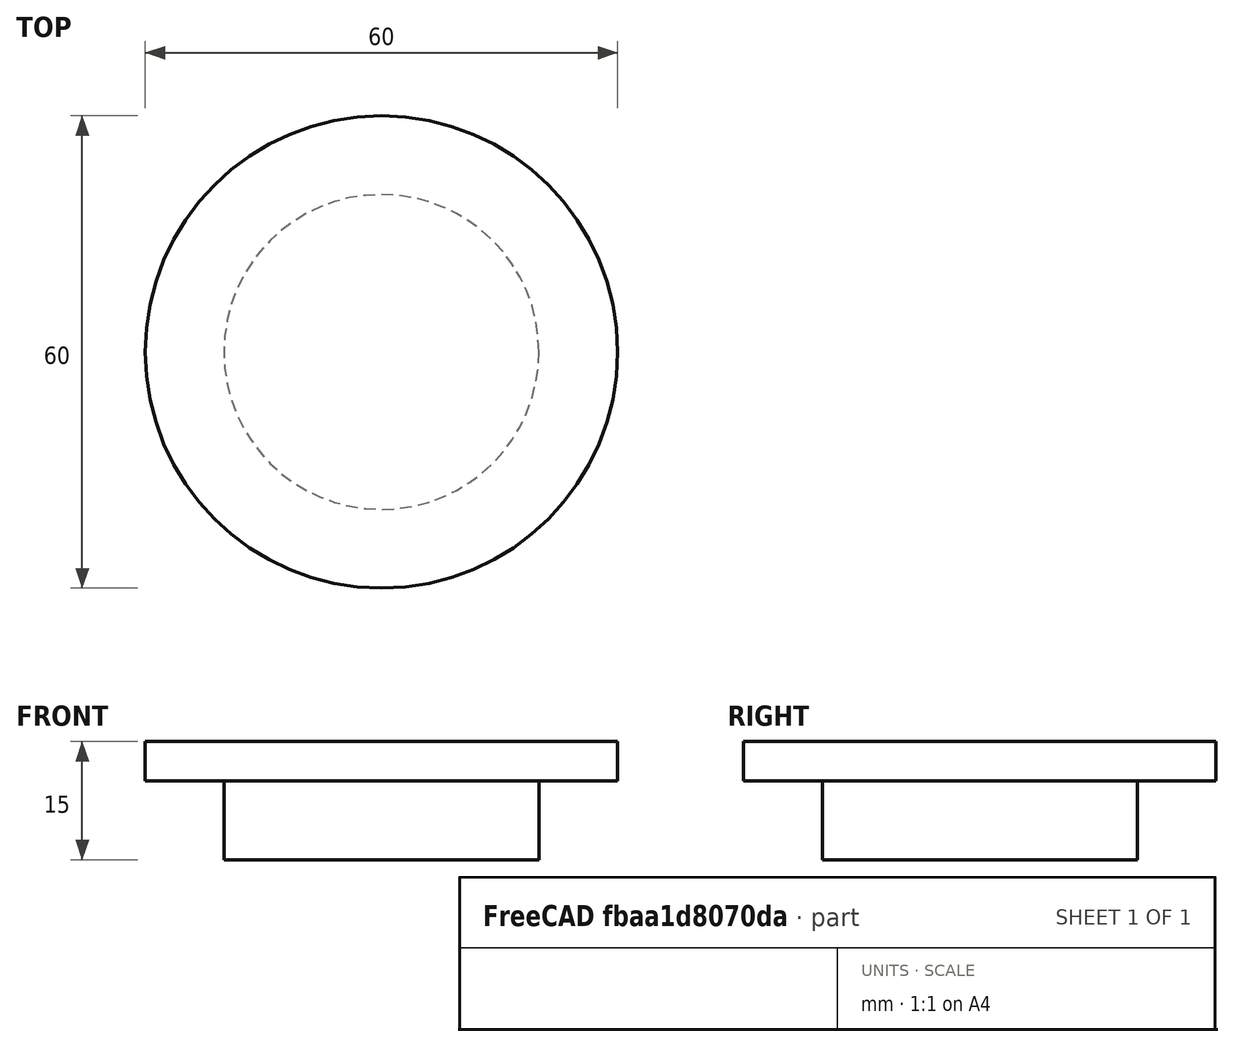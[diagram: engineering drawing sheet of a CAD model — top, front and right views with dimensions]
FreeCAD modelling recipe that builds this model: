
FCSTD DOCUMENT  (FreeCAD 0.18R4 (GitTag))
Label: Ariel Lid
License: All rights reserved
LicenseURL: http://en.wikipedia.org/wiki/All_rights_reserved
objects: Sketcher::SketchObject×2, PartDesign::Pad×2, PartDesign::Body×1, Mesh::Feature×1
note: 7 computed .brp shape members not serialized (recipe doc carries the construction recipe); baked Part::Feature solids carry a one-line shape summary decoded from their .brp

FEATURE [Sketcher::SketchObject] Sketch
  sketch-geometry (1):
    g0: Circle CenterX=0 CenterY=0 CenterZ=0 NormalX=0 NormalY=0 NormalZ=1 AngleXU=0 Radius=30
  constraints (2):
    c: Radius(g0) = 30
    c: Coincident(g0,g-1)
FEATURE [PartDesign::Pad] Pad
  Length = 5
  Length2 = 100
  Profile = -> Sketch
  Type = 0
FEATURE [Sketcher::SketchObject] Sketch001
  MapMode = 5
  Support = -> [XY_Plane]
  sketch-geometry (1):
    g0: Circle CenterX=0 CenterY=0 CenterZ=0 NormalX=0 NormalY=0 NormalZ=1 AngleXU=0 Radius=20
  constraints (2):
    c: Coincident(g0,g-1)
    c: Radius(g0) = 20
FEATURE [PartDesign::Pad] Pad001
  BaseFeature = -> Pad
  Length = 10
  Length2 = 100
  Profile = -> Sketch001
  Reversed = true
  Type = 0
FEATURE [PartDesign::Body] Body
  Group = -> [Sketch,Pad,Sketch001,Pad001]
  Origin = -> Origin
  Tip = -> Pad001
FEATURE [Mesh::Feature] Mesh  label="Body (Meshed)"
